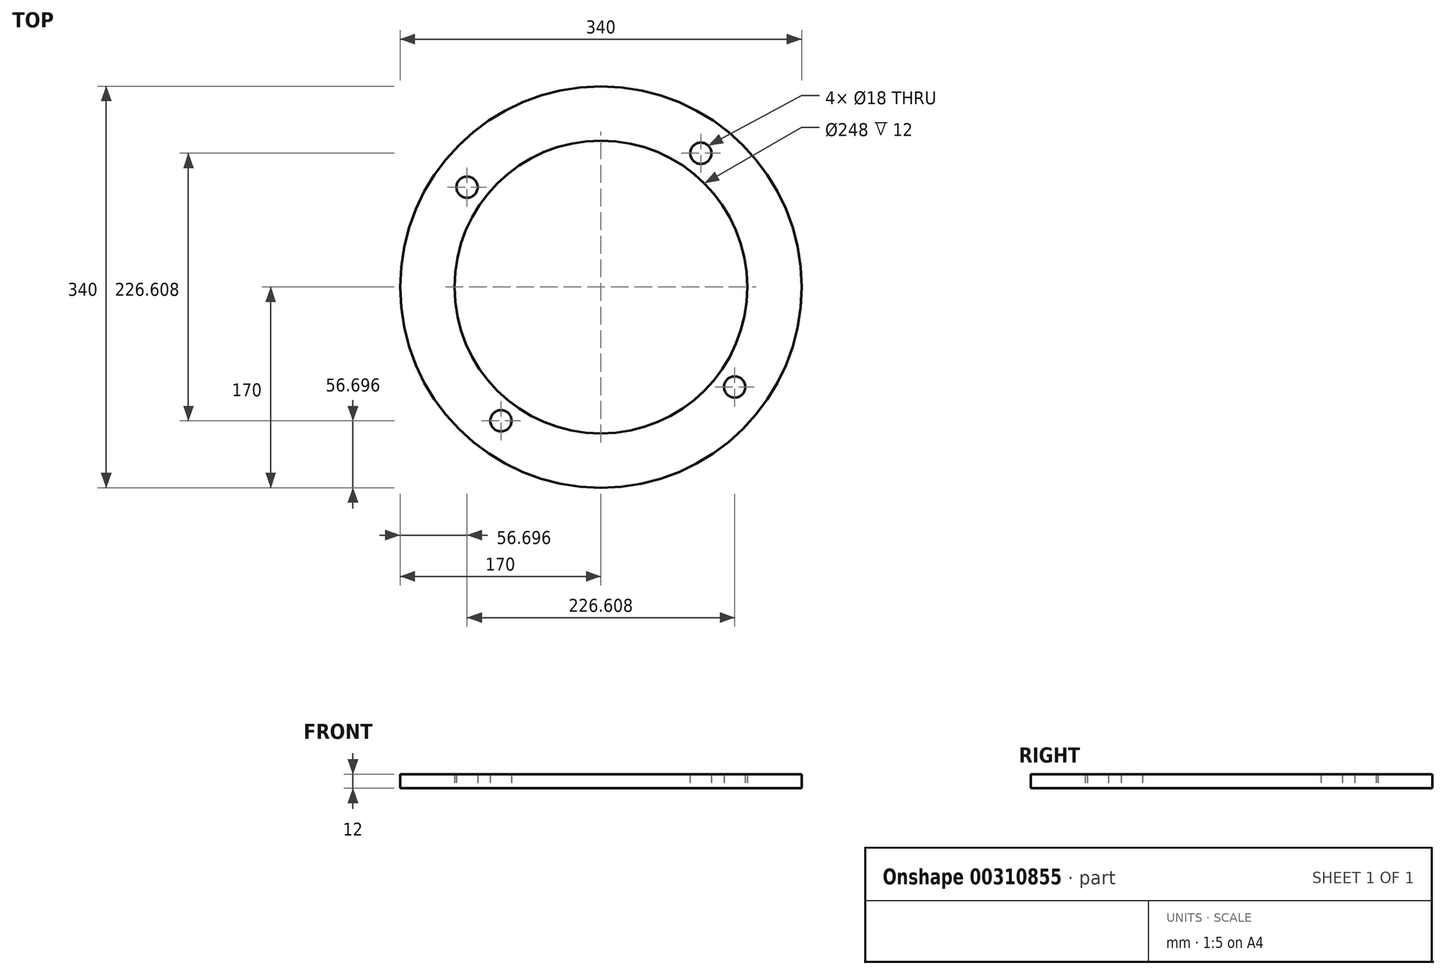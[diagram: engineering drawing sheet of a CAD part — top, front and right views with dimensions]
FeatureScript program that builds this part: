
annotation { "Feature Type Name" : "Feature", "Feature Type Description" : "" }
export const myFeature = defineFeature(function(context is Context, id is Id, definition is map)
    precondition{}
    {
        {
            var Q0;
            Q0=qCreatedBy(makeId("Top.planeOp"),FACE);
            var sketch = newSketch(context, id + "F0", { "sketchPlane" : qUnion([Q0])});
            skCircle(sketch, "E0", {"center": v(0, 0) * mm, "radius": 170 * mm});
            skCircle(sketch, "E1", {"center": v(0, 0) * mm, "radius": 124 * mm});
            skCircle(sketch, "E2", {"center": v(0, 0) * mm, "radius": 141.42 * mm, "construction": true});
            skCircle(sketch, "E3", {"center": v(-113.3, 84.63) * mm, "radius": 9 * mm});
            skCircle(sketch, "E4.1.0", {"center": v(-84.63, -113.3) * mm, "radius": 9 * mm});
            skCircle(sketch, "E4.2.0", {"center": v(113.3, -84.63) * mm, "radius": 9 * mm});
            skCircle(sketch, "E5.1.3.0", {"center": v(84.63, 113.3) * mm, "radius": 9 * mm});
            skSolve(sketch);
        }
        {
            var Q0;
            Q0=makeQuery(id+"F0.imprint","IMPRINT",FACE,{"disambiguationData":[TD([[makeQuery(id+"F0.imprint","IMPRINT",EDGE,{"derivedFrom":sQuery(id+"F0.wireOp",EDGE,"E0")}),1.0]])]});
            extrude(context, id + "F1", {"entities" : qUnion([Q0]), "depth" : 12 * mm});
        }
    });
